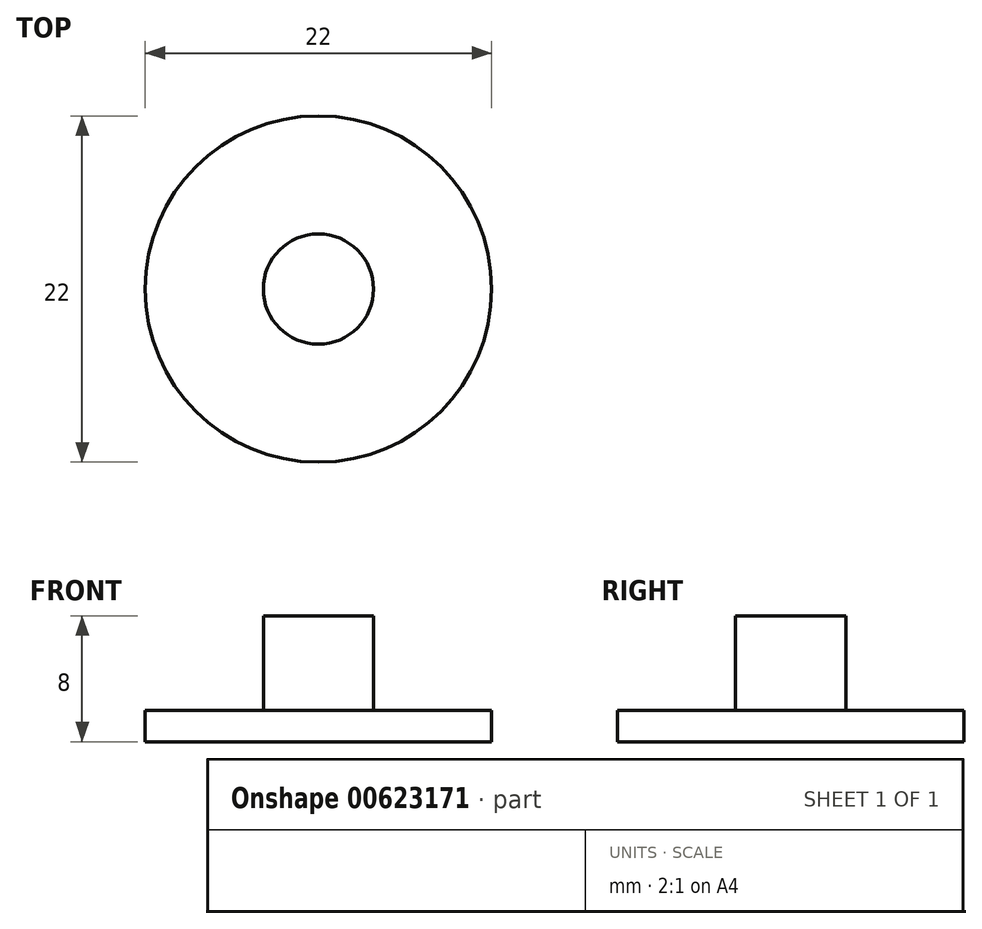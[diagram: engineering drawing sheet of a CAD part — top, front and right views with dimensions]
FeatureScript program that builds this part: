
annotation { "Feature Type Name" : "Feature", "Feature Type Description" : "" }
export const myFeature = defineFeature(function(context is Context, id is Id, definition is map)
    precondition{}
    {
        {
            var Q0;
            Q0=qCreatedBy(makeId("Top.planeOp"),FACE);
            var sketch = newSketch(context, id + "F0", { "sketchPlane" : qUnion([Q0])});
            skCircle(sketch, "E0", {"center": v(0, 0) * mm, "radius": 3.5 * mm});
            skSolve(sketch);
        }
        {
            var Q0;
            Q0=makeQuery(id+"F0.imprint","IMPRINT",FACE,{"disambiguationData":[TD([[makeQuery(id+"F0.imprint","IMPRINT",EDGE,{"derivedFrom":sQuery(id+"F0.wireOp",EDGE,"E0")}),1.0]])]});
            extrude(context, id + "F1", {"entities" : qUnion([Q0]), "depth" : 6 * mm, "offsetDistance" : 25 * mm});
        }
        {
            var Q0;
            Q0=makeQuery(id+"F1.opExtrude","CAP_FACE",FACE,{"disambiguationData":[OSD([sQuery(id+"F0.wireOp",EDGE,"E0")])],"isStart":true});
            var sketch = newSketch(context, id + "F2", { "sketchPlane" : qUnion([Q0])});
            skCircle(sketch, "E1", {"center": v(0, 0) * mm, "radius": 11 * mm});
            skSolve(sketch);
        }
        {
            var Q0;
            Q0=makeQuery(id+"F2.imprint","IMPRINT",FACE,{"disambiguationData":[TD([[makeQuery(id+"F2.imprint","IMPRINT",EDGE,{"derivedFrom":makeQuery(id+"F1.opExtrude","CAP_EDGE",EDGE,{"disambiguationData":[OSD([sQuery(id+"F0.wireOp",EDGE,"E0")])],"isStart":false})}),1.0]])]});
            var Q1;
            Q1=makeQuery(id+"F2.imprint","IMPRINT",FACE,{"disambiguationData":[TD([[makeQuery(id+"F2.imprint","IMPRINT",EDGE,{"derivedFrom":sQuery(id+"F2.wireOp",EDGE,"E1")}),1.0]])]});
            var Q2;
            Q2=makeQuery(id+"F2.imprint","IMPRINT",FACE,{"disambiguationData":[TD([[makeQuery(id+"F2.imprint","IMPRINT",EDGE,{"derivedFrom":makeQuery(id+"F1.opExtrude","CAP_EDGE",EDGE,{"disambiguationData":[OSD([sQuery(id+"F0.wireOp",EDGE,"E0")])],"isStart":true})}),-1.0]])]});
            extrude(context, id + "F3", {"entities" : qUnion([Q0, Q1, Q2]), "operationType" : NewBodyOperationType.ADD, "depth" : 2 * mm, "offsetDistance" : 25 * mm});
        }
    });
